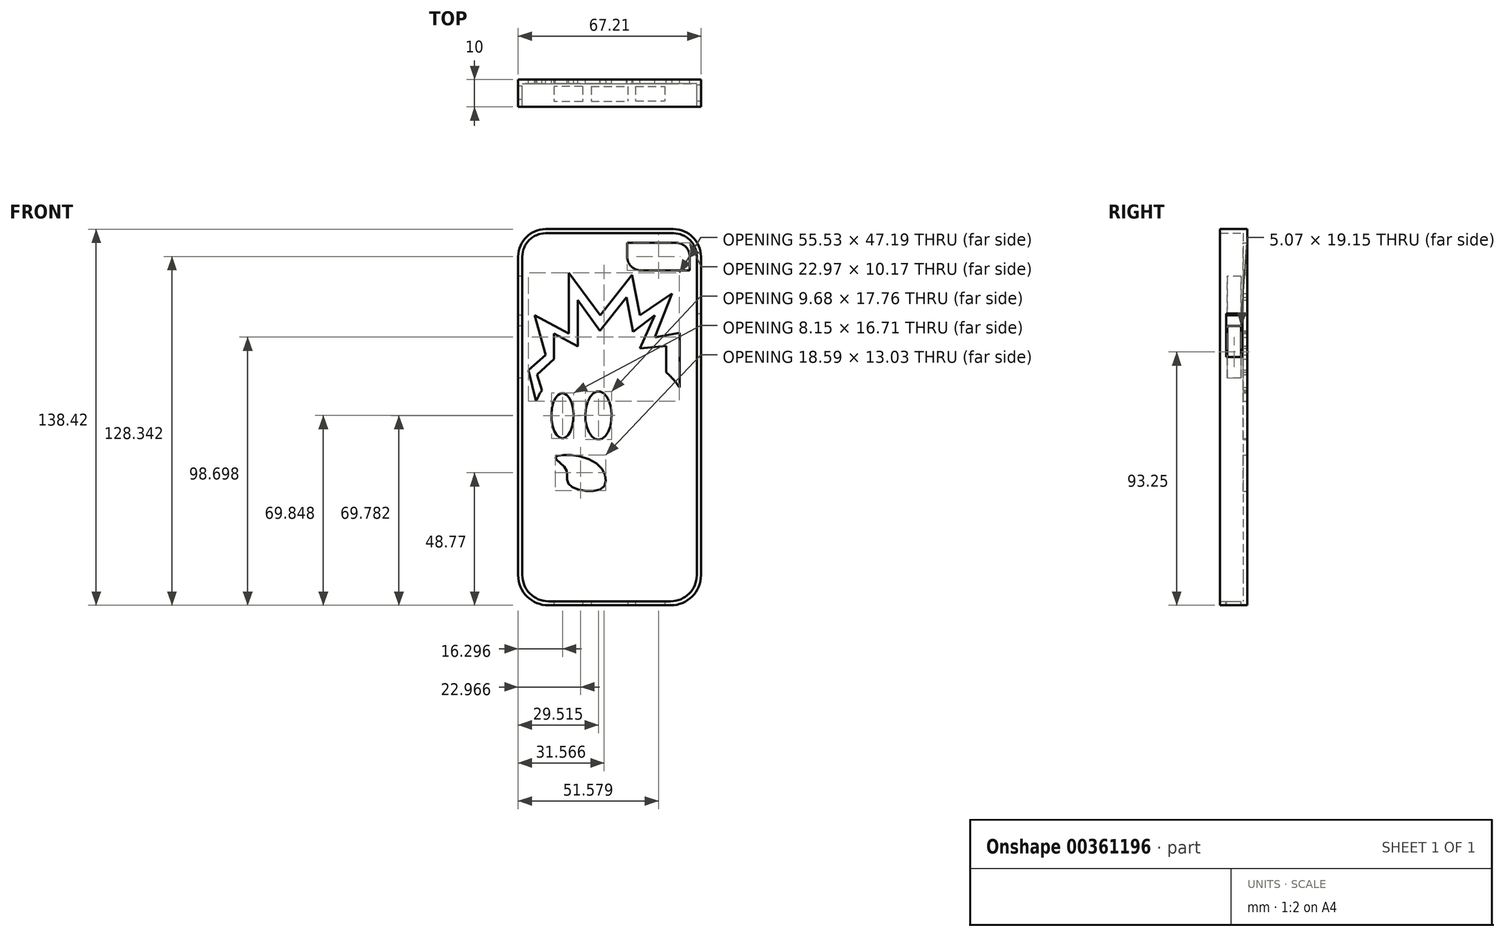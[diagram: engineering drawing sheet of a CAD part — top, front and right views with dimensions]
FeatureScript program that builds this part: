
annotation { "Feature Type Name" : "Feature", "Feature Type Description" : "" }
export const myFeature = defineFeature(function(context is Context, id is Id, definition is map)
    precondition{}
    {
        {
            var Q0;
            Q0=qCreatedBy(makeId("Front.planeOp"),FACE);
            var sketch = newSketch(context, id + "F0", { "sketchPlane" : qUnion([Q0])});
            skLineSegment(sketch, "E0.bottom", {"start": v(-25.06, 51.88) * mm, "end": v(21.95, 51.88) * mm});
            skLineSegment(sketch, "E0.top", {"start": v(-24.06, -86.54) * mm, "end": v(20.95, -86.54) * mm});
            skLineSegment(sketch, "E0.left", {"start": v(-35.16, 41.78) * mm, "end": v(-35.16, -75.44) * mm});
            skLineSegment(sketch, "E0.right", {"start": v(32.05, 41.78) * mm, "end": v(32.05, -75.44) * mm});
            skPoint(sketch, "E1.visualSharp", {"position": v(-35.16, 51.88) * mm});
            skArc(sketch, "E1.filletArc", {"start": v(-25.06, 51.88) * mm, "mid": v(-32.2, 48.92) * mm, "end": v(-35.16, 41.78) * mm});
            skPoint(sketch, "E2.visualSharp", {"position": v(32.05, 51.88) * mm});
            skArc(sketch, "E2.filletArc", {"start": v(32.05, 41.78) * mm, "mid": v(29.1, 48.92) * mm, "end": v(21.95, 51.88) * mm});
            skPoint(sketch, "E3.visualSharp", {"position": v(-35.16, -86.54) * mm});
            skArc(sketch, "E3.filletArc", {"start": v(-35.16, -75.44) * mm, "mid": v(-31.9, -83.29) * mm, "end": v(-24.06, -86.54) * mm});
            skPoint(sketch, "E4.visualSharp", {"position": v(32.05, -86.54) * mm});
            skArc(sketch, "E4.filletArc", {"start": v(20.95, -86.54) * mm, "mid": v(28.8, -83.29) * mm, "end": v(32.05, -75.44) * mm});
            skSolve(sketch);
        }
        {
            var Q0;
            Q0 = qSketchRegion(id + "F0", true);
            extrude(context, id + "F1", {"entities" : qUnion([Q0]), "depth" : 10 * mm});
        }
        {
            var Q0;
            Q0=makeQuery(id+"F1.opExtrude","CAP_FACE",FACE,{"disambiguationData":[OSD([sQuery(id+"F0.wireOp",EDGE,"E0.bottom"),sQuery(id+"F0.wireOp",EDGE,"E0.top"),sQuery(id+"F0.wireOp",EDGE,"E0.left"),sQuery(id+"F0.wireOp",EDGE,"E0.right"),sQuery(id+"F0.wireOp",EDGE,"E1.filletArc"),sQuery(id+"F0.wireOp",EDGE,"E2.filletArc"),sQuery(id+"F0.wireOp",EDGE,"E3.filletArc"),sQuery(id+"F0.wireOp",EDGE,"E4.filletArc")])],"isStart":false});
            shell(context, id + "F2", {"entities" : qUnion([Q0]), "thickness" : 2.5 * mm});
        }
        {
            var Q0;
            Q0=qCreatedBy(makeId("Front.planeOp"),FACE);
            var sketch = newSketch(context, id + "F3", { "sketchPlane" : qUnion([Q0])});
            skLineSegment(sketch, "E5.bottom", {"start": v(3.35, 45.15) * mm, "end": v(25.55, 45.15) * mm});
            skLineSegment(sketch, "E5.top", {"start": v(3.35, 35.18) * mm, "end": v(25.55, 35.18) * mm});
            skLineSegment(sketch, "E5.left", {"start": v(3.35, 45.15) * mm, "end": v(3.35, 35.18) * mm});
            skLineSegment(sketch, "E5.right", {"start": v(25.55, 45.15) * mm, "end": v(25.55, 35.18) * mm});
            skSolve(sketch);
        }
        {
            var Q0;
            Q0=makeQuery(id+"F2.opShell","OFFSET_FACE",FACE,{"disambiguationData":[OSD([sQuery(id+"F0.wireOp",EDGE,"E0.bottom"),sQuery(id+"F0.wireOp",EDGE,"E0.top"),sQuery(id+"F0.wireOp",EDGE,"E0.left"),sQuery(id+"F0.wireOp",EDGE,"E0.right"),sQuery(id+"F0.wireOp",EDGE,"E1.filletArc"),sQuery(id+"F0.wireOp",EDGE,"E2.filletArc"),sQuery(id+"F0.wireOp",EDGE,"E3.filletArc"),sQuery(id+"F0.wireOp",EDGE,"E4.filletArc")])]});
            var Q1;
            Q1=sQuery(id+"F3.wireOp",EDGE,"E5.bottom");
            var Q2;
            Q2=sQuery(id+"F3.wireOp",EDGE,"E5.left");
            var Q3;
            Q3=sQuery(id+"F3.wireOp",EDGE,"E5.top");
            var Q4;
            Q4=sQuery(id+"F3.wireOp",EDGE,"E5.right");
            extrude(context, id + "F4", {"entities" : qUnion([Q0]), "operationType" : NewBodyOperationType.REMOVE, "surfaceEntities" : qUnion([Q1, Q2, Q3, Q4]), "oppositeDirection" : true, "depth" : 25 * mm});
        }
        {
            var Q0;
            Q0 = qSketchRegion(id + "F0", true);
            extrude(context, id + "F5", {"entities" : qUnion([Q0]), "operationType" : NewBodyOperationType.ADD, "depth" : 10 * mm});
        }
        {
            var Q0;
            Q0 = qSketchRegion(id + "F0", true);
            extrude(context, id + "F6", {"entities" : qUnion([Q0]), "operationType" : NewBodyOperationType.ADD, "depth" : 10 * mm});
        }
        {
            var Q0;
            Q0=makeQuery(id+"F5.opExtrude","CAP_FACE",FACE,{"disambiguationData":[OSD([sQuery(id+"F0.wireOp",EDGE,"E0.bottom"),sQuery(id+"F0.wireOp",EDGE,"E0.top"),sQuery(id+"F0.wireOp",EDGE,"E0.left"),sQuery(id+"F0.wireOp",EDGE,"E0.right"),sQuery(id+"F0.wireOp",EDGE,"E1.filletArc"),sQuery(id+"F0.wireOp",EDGE,"E2.filletArc"),sQuery(id+"F0.wireOp",EDGE,"E3.filletArc"),sQuery(id+"F0.wireOp",EDGE,"E4.filletArc"),sQuery(id+"F0.wireOp",EDGE,"3Y9CP9Op-mfTd-9fag-K7uA-JU66n6fimk0H.bottom"),sQuery(id+"F0.wireOp",EDGE,"3Y9CP9Op-mfTd-9fag-K7uA-JU66n6fimk0H.top"),sQuery(id+"F0.wireOp",EDGE,"3Y9CP9Op-mfTd-9fag-K7uA-JU66n6fimk0H.left"),sQuery(id+"F0.wireOp",EDGE,"3Y9CP9Op-mfTd-9fag-K7uA-JU66n6fimk0H.right"),sQuery(id+"F0.wireOp",EDGE,"22cb3f92-145b-4dae-ab03-714529ae1dc0.filletArc"),sQuery(id+"F0.wireOp",EDGE,"73148f33-a80d-44ac-9ddb-d84ddd6c341a.filletArc")])],"isStart":false});
            shell(context, id + "F7", {"entities" : qUnion([Q0]), "thickness" : 1.5 * mm});
        }
        {
            var Q0;
            Q0=makeQuery(id+"F1.opExtrude","SWEPT_FACE",FACE,{"disambiguationData":[OSD([sQuery(id+"F0.wireOp",EDGE,"E0.left")])]});
            var sketch = newSketch(context, id + "F8", { "sketchPlane" : qUnion([Q0])});
            skLineSegment(sketch, "E6.bottom", {"start": v(2.3, 20.23) * mm, "end": v(7.36, 20.23) * mm});
            skLineSegment(sketch, "E6.top", {"start": v(2.3, 34.6) * mm, "end": v(7.36, 34.6) * mm});
            skLineSegment(sketch, "E6.left", {"start": v(2.3, 20.23) * mm, "end": v(2.3, 34.6) * mm});
            skLineSegment(sketch, "E6.right", {"start": v(7.36, 20.23) * mm, "end": v(7.36, 34.6) * mm});
            skLineSegment(sketch, "E7.bottom", {"start": v(2.3, -2.87) * mm, "end": v(7.36, -2.87) * mm});
            skLineSegment(sketch, "E7.top", {"start": v(2.3, 16.29) * mm, "end": v(7.36, 16.29) * mm});
            skLineSegment(sketch, "E7.left", {"start": v(2.3, -2.87) * mm, "end": v(2.3, 16.29) * mm});
            skLineSegment(sketch, "E7.right", {"start": v(7.36, -2.87) * mm, "end": v(7.36, 16.29) * mm});
            skSolve(sketch);
        }
        {
            var Q0;
            Q0=makeQuery(id+"F8.imprint","IMPRINT",FACE,{"disambiguationData":[TD([[makeQuery(id+"F8.imprint","IMPRINT",EDGE,{"derivedFrom":sQuery(id+"F8.wireOp",EDGE,"E7.bottom")}),1.0]])]});
            var Q1;
            Q1=makeQuery(id+"F8.imprint","IMPRINT",FACE,{"disambiguationData":[TD([[makeQuery(id+"F8.imprint","IMPRINT",EDGE,{"derivedFrom":sQuery(id+"F8.wireOp",EDGE,"E6.bottom")}),1.0]])]});
            extrude(context, id + "F9", {"entities" : qUnion([Q0, Q1]), "operationType" : NewBodyOperationType.REMOVE, "oppositeDirection" : true, "depth" : 25 * mm});
        }
        {
            var Q0;
            Q0=makeQuery(id+"F1.opExtrude","SWEPT_FACE",FACE,{"disambiguationData":[OSD([sQuery(id+"F0.wireOp",EDGE,"E0.top")])]});
            var sketch = newSketch(context, id + "F10", { "sketchPlane" : qUnion([Q0])});
            skLineSegment(sketch, "E8.bottom", {"start": v(-11.51, 2.49) * mm, "end": v(-22.04, 2.49) * mm});
            skLineSegment(sketch, "E8.top", {"start": v(-11.51, 8.07) * mm, "end": v(-22.04, 8.07) * mm});
            skLineSegment(sketch, "E8.left", {"start": v(-11.51, 2.49) * mm, "end": v(-11.51, 8.07) * mm});
            skLineSegment(sketch, "E8.right", {"start": v(-22.04, 2.49) * mm, "end": v(-22.04, 8.07) * mm});
            skLineSegment(sketch, "E9.bottom", {"start": v(-8.33, 2.49) * mm, "end": v(5.23, 2.49) * mm});
            skLineSegment(sketch, "E9.top", {"start": v(-8.33, 7.94) * mm, "end": v(5.23, 7.94) * mm});
            skLineSegment(sketch, "E9.left", {"start": v(-8.33, 2.49) * mm, "end": v(-8.33, 7.94) * mm});
            skLineSegment(sketch, "E9.right", {"start": v(5.23, 2.49) * mm, "end": v(5.23, 7.94) * mm});
            skPoint(sketch, "E9.middle.positionSnap0", {"position": v(-1.55, 10) * mm});
            skPoint(sketch, "E9.centerSnap0", {"position": v(-1.55, 10) * mm});
            skLineSegment(sketch, "E10.bottom", {"start": v(8.01, 2.49) * mm, "end": v(18.78, 2.49) * mm});
            skLineSegment(sketch, "E10.top", {"start": v(8.01, 7.83) * mm, "end": v(18.78, 7.83) * mm});
            skLineSegment(sketch, "E10.left", {"start": v(8.01, 2.49) * mm, "end": v(8.01, 7.83) * mm});
            skLineSegment(sketch, "E10.right", {"start": v(18.78, 2.49) * mm, "end": v(18.78, 7.83) * mm});
            skSolve(sketch);
        }
        {
            var Q0;
            Q0=makeQuery(id+"F10.imprint","IMPRINT",FACE,{"disambiguationData":[TD([[makeQuery(id+"F10.imprint","IMPRINT",EDGE,{"derivedFrom":sQuery(id+"F10.wireOp",EDGE,"E8.bottom")}),-1.0]])]});
            var Q1;
            Q1=makeQuery(id+"F10.imprint","IMPRINT",FACE,{"disambiguationData":[TD([[makeQuery(id+"F10.imprint","IMPRINT",EDGE,{"derivedFrom":sQuery(id+"F10.wireOp",EDGE,"E9.bottom")}),1.0]])]});
            var Q2;
            Q2=makeQuery(id+"F10.imprint","IMPRINT",FACE,{"disambiguationData":[TD([[makeQuery(id+"F10.imprint","IMPRINT",EDGE,{"derivedFrom":sQuery(id+"F10.wireOp",EDGE,"E10.bottom")}),1.0]])]});
            extrude(context, id + "F11", {"entities" : qUnion([Q0, Q1, Q2]), "operationType" : NewBodyOperationType.REMOVE, "oppositeDirection" : true, "depth" : 25 * mm});
        }
        {
            var Q0;
            Q0=makeQuery(id+"F1.opExtrude","SWEPT_FACE",FACE,{"disambiguationData":[OSD([sQuery(id+"F0.wireOp",EDGE,"E0.right")])]});
            var sketch = newSketch(context, id + "F12", { "sketchPlane" : qUnion([Q0])});
            skLineSegment(sketch, "E11.bottom", {"start": v(-7.79, 4.8) * mm, "end": v(-1.88, 4.8) * mm});
            skLineSegment(sketch, "E11.top", {"start": v(-7.79, 20.88) * mm, "end": v(-1.88, 20.88) * mm});
            skLineSegment(sketch, "E11.left", {"start": v(-7.79, 4.8) * mm, "end": v(-7.79, 20.88) * mm});
            skLineSegment(sketch, "E11.right", {"start": v(-1.88, 4.8) * mm, "end": v(-1.88, 20.88) * mm});
            skSolve(sketch);
        }
        {
            var Q0;
            Q0=makeQuery(id+"F12.imprint","IMPRINT",FACE,{"disambiguationData":[TD([[makeQuery(id+"F12.imprint","IMPRINT",EDGE,{"derivedFrom":sQuery(id+"F12.wireOp",EDGE,"E11.bottom")}),1.0]])]});
            extrude(context, id + "F13", {"entities" : qUnion([Q0]), "operationType" : NewBodyOperationType.REMOVE, "oppositeDirection" : true, "depth" : 10 * mm});
        }
        {
            var Q0;
            {var subQ0=sQuery(id+"F0.wireOp",EDGE,"73148f33-a80d-44ac-9ddb-d84ddd6c341a.filletArc");var subQ1=sQuery(id+"F0.wireOp",EDGE,"22cb3f92-145b-4dae-ab03-714529ae1dc0.filletArc");var subQ2=sQuery(id+"F0.wireOp",EDGE,"3Y9CP9Op-mfTd-9fag-K7uA-JU66n6fimk0H.right");var subQ3=sQuery(id+"F0.wireOp",EDGE,"3Y9CP9Op-mfTd-9fag-K7uA-JU66n6fimk0H.left");var subQ4=sQuery(id+"F0.wireOp",EDGE,"3Y9CP9Op-mfTd-9fag-K7uA-JU66n6fimk0H.top");var subQ5=sQuery(id+"F0.wireOp",EDGE,"3Y9CP9Op-mfTd-9fag-K7uA-JU66n6fimk0H.bottom");var subQ6=sQuery(id+"F0.wireOp",EDGE,"E4.filletArc");var subQ7=sQuery(id+"F0.wireOp",EDGE,"E3.filletArc");var subQ8=sQuery(id+"F0.wireOp",EDGE,"E2.filletArc");var subQ9=sQuery(id+"F0.wireOp",EDGE,"E1.filletArc");var subQ10=sQuery(id+"F0.wireOp",EDGE,"E0.right");var subQ11=sQuery(id+"F0.wireOp",EDGE,"E0.left");var subQ12=sQuery(id+"F0.wireOp",EDGE,"E0.top");var subQ13=sQuery(id+"F0.wireOp",EDGE,"E0.bottom");Q0=makeQuery(id+"F5.boolean.opBoolean","MERGE",FACE,{"derivedFrom":[makeQuery(id+"F1.opExtrude","CAP_FACE",FACE,{"disambiguationData":[OSD([subQ13,subQ12,subQ11,subQ10,subQ9,subQ8,subQ7,subQ6,subQ5,subQ4,subQ3,subQ2,subQ1,subQ0])],"isStart":true}),makeQuery(id+"F5.opExtrude","CAP_FACE",FACE,{"disambiguationData":[OSD([subQ13,subQ12,subQ11,subQ10,subQ9,subQ8,subQ7,subQ6,subQ5,subQ4,subQ3,subQ2,subQ1,subQ0])],"isStart":true})]});}
            var sketch = newSketch(context, id + "F14", { "sketchPlane" : qUnion([Q0])});
            skPoint(sketch, "E12.endSnap0", {"position": v(19.8, -6.18) * mm});
            skLineSegment(sketch, "E13.bottom", {"start": v(-4.94, 46.89) * mm, "end": v(-22.9, 46.89) * mm});
            skLineSegment(sketch, "E13.top", {"start": v(-9.94, 36.72) * mm, "end": v(-27.9, 36.72) * mm});
            skLineSegment(sketch, "E13.left", {"start": v(-4.94, 46.89) * mm, "end": v(-4.94, 41.72) * mm});
            skLineSegment(sketch, "E13.right", {"start": v(-27.9, 41.89) * mm, "end": v(-27.9, 36.72) * mm});
            skPoint(sketch, "E14.visualSharp", {"position": v(-4.94, 36.72) * mm});
            skArc(sketch, "E14.filletArc", {"start": v(-9.94, 36.72) * mm, "mid": v(-6.4, 38.18) * mm, "end": v(-4.94, 41.72) * mm});
            skPoint(sketch, "E15.visualSharp", {"position": v(-27.9, 46.89) * mm});
            skArc(sketch, "E15.filletArc", {"start": v(-22.9, 46.89) * mm, "mid": v(-26.44, 45.42) * mm, "end": v(-27.9, 41.89) * mm});
            skSolve(sketch);
        }
        {
            var Q0;
            Q0 = qSketchRegion(id + "F14", true);
            extrude(context, id + "F15", {"entities" : qUnion([Q0]), "operationType" : NewBodyOperationType.REMOVE, "oppositeDirection" : true, "depth" : 25 * mm});
        }
        {
            var Q0;
            {var subQ0=sQuery(id+"F0.wireOp",EDGE,"E4.filletArc");var subQ1=sQuery(id+"F0.wireOp",EDGE,"E3.filletArc");var subQ2=sQuery(id+"F0.wireOp",EDGE,"E2.filletArc");var subQ3=sQuery(id+"F0.wireOp",EDGE,"E1.filletArc");var subQ4=sQuery(id+"F0.wireOp",EDGE,"E0.right");var subQ5=sQuery(id+"F0.wireOp",EDGE,"E0.left");var subQ6=sQuery(id+"F0.wireOp",EDGE,"E0.top");var subQ7=sQuery(id+"F0.wireOp",EDGE,"E0.bottom");Q0=makeQuery(id+"F5.boolean.opBoolean","MERGE",FACE,{"derivedFrom":[makeQuery(id+"F1.opExtrude","CAP_FACE",FACE,{"disambiguationData":[OSD([subQ7,subQ6,subQ5,subQ4,subQ3,subQ2,subQ1,subQ0])],"isStart":true}),makeQuery(id+"F5.opExtrude","CAP_FACE",FACE,{"disambiguationData":[OSD([subQ7,subQ6,subQ5,subQ4,subQ3,subQ2,subQ1,subQ0])],"isStart":true})]});}
            var sketch = newSketch(context, id + "F16", { "sketchPlane" : qUnion([Q0])});
            skCircle(sketch, "E16", {"center": v(0.8, -23.34) * mm, "radius": 30.22 * mm});
            skLineSegment(sketch, "E17", {"start": v(-24.17, -6.32) * mm, "end": v(-24.17, 13.76) * mm});
            skLineSegment(sketch, "E18", {"start": v(-15.1, 12.09) * mm, "end": v(-21.49, 28.2) * mm});
            skLineSegment(sketch, "E19", {"start": v(-21.49, 28.2) * mm, "end": v(-9.58, 20.16) * mm});
            skLineSegment(sketch, "E20", {"start": v(-9.58, 20.16) * mm, "end": v(-6.72, 35.1) * mm});
            skLineSegment(sketch, "E21", {"start": v(-6.72, 35.1) * mm, "end": v(5.04, 20.16) * mm});
            skLineSegment(sketch, "E22", {"start": v(5.04, 20.16) * mm, "end": v(16.59, 35.76) * mm});
            skLineSegment(sketch, "E23", {"start": v(16.59, 35.76) * mm, "end": v(16.59, 13.44) * mm});
            skLineSegment(sketch, "E24", {"start": v(16.59, 13.44) * mm, "end": v(29.06, 20.16) * mm});
            skLineSegment(sketch, "E25", {"start": v(29.06, 20.16) * mm, "end": v(25.06, 5.56) * mm});
            skLineSegment(sketch, "E26", {"start": v(25.06, 5.56) * mm, "end": v(31.36, -0.02) * mm});
            skLineSegment(sketch, "E27", {"start": v(31.36, -0.02) * mm, "end": v(28.58, -11.44) * mm});
            skLineSegment(sketch, "E28", {"start": v(-24.17, 13.76) * mm, "end": v(-15.1, 12.09) * mm});
            skLineSegment(sketch, "E29", {"start": v(-19.22, -0.7) * mm, "end": v(-19.22, 8.84) * mm});
            skLineSegment(sketch, "E30", {"start": v(-19.22, 8.84) * mm, "end": v(-9.58, 7.96) * mm});
            skLineSegment(sketch, "E31", {"start": v(-9.58, 7.96) * mm, "end": v(-15.1, 20.16) * mm});
            skLineSegment(sketch, "E32", {"start": v(-15.1, 20.16) * mm, "end": v(-7.02, 14.06) * mm});
            skPoint(sketch, "E32.endSnap0", {"position": v(-12.34, 14.06) * mm});
            skLineSegment(sketch, "E33", {"start": v(-7.02, 14.06) * mm, "end": v(-4.66, 26.83) * mm});
            skLineSegment(sketch, "E34", {"start": v(-4.66, 26.83) * mm, "end": v(5.1, 14.42) * mm});
            skLineSegment(sketch, "E35", {"start": v(5.1, 14.42) * mm, "end": v(13.27, 25.79) * mm});
            skLineSegment(sketch, "E36", {"start": v(13.27, 25.79) * mm, "end": v(13.27, 8.74) * mm});
            skLineSegment(sketch, "E37", {"start": v(13.27, 8.74) * mm, "end": v(21.98, 13.44) * mm});
            skLineSegment(sketch, "E38", {"start": v(21.98, 13.44) * mm, "end": v(21.98, 4.05) * mm});
            skLineSegment(sketch, "E39", {"start": v(21.98, 4.05) * mm, "end": v(28.2, -1.65) * mm});
            skPoint(sketch, "E39.endSnap0", {"position": v(28.2, 2.77) * mm});
            skLineSegment(sketch, "E40", {"start": v(28.2, -1.65) * mm, "end": v(26.42, -7.32) * mm});
            skEllipse(sketch, "E41", {"center": v(18.86, -16.76) * mm, "majorRadius": 8.36 * mm, "minorRadius": 4.07 * mm, "majorAxis": v(0, -1)});
            skEllipse(sketch, "E42", {"center": v(5.65, -16.7) * mm, "majorRadius": 8.88 * mm, "minorRadius": 4.84 * mm, "majorAxis": v(0, -1)});
            skFitSpline(sketch, "E43", {"points": [v(21.49, -32.18) * mm, v(7.05, -33.82) * mm, v(4.16, -43.35) * mm, v(16.46, -42.02) * mm, v(17.55, -36.44) * mm, v(21.49, -32.18) * mm]});
            skSolve(sketch);
        }
        {
            var Q0;
            {var subQ2=sQuery(id+"F16.wireOp",EDGE,"E17");Q0=makeQuery(id+"F16.imprint","IMPRINT",FACE,{"disambiguationData":[TD([[makeQuery(id+"F16.imprint","IMPRINT",EDGE,{"derivedFrom":subQ2}),-1.0]])]});}
            var Q1;
            Q1=makeQuery(id+"F16.imprint","IMPRINT",FACE,{"disambiguationData":[TD([[makeQuery(id+"F16.imprint","IMPRINT",EDGE,{"derivedFrom":sQuery(id+"F16.wireOp",EDGE,"E42")}),1.0]])]});
            var Q2;
            Q2=makeQuery(id+"F16.imprint","IMPRINT",FACE,{"disambiguationData":[TD([[makeQuery(id+"F16.imprint","IMPRINT",EDGE,{"derivedFrom":sQuery(id+"F16.wireOp",EDGE,"E41")}),1.0]])]});
            var Q3;
            Q3=makeQuery(id+"F16.imprint","IMPRINT",FACE,{"disambiguationData":[TD([[makeQuery(id+"F16.imprint","IMPRINT",EDGE,{"derivedFrom":sQuery(id+"F16.wireOp",EDGE,"E43")}),1.0]])]});
            extrude(context, id + "F17", {"entities" : qUnion([Q0, Q1, Q2, Q3]), "operationType" : NewBodyOperationType.REMOVE, "oppositeDirection" : true, "depth" : 25 * mm});
        }
    });
